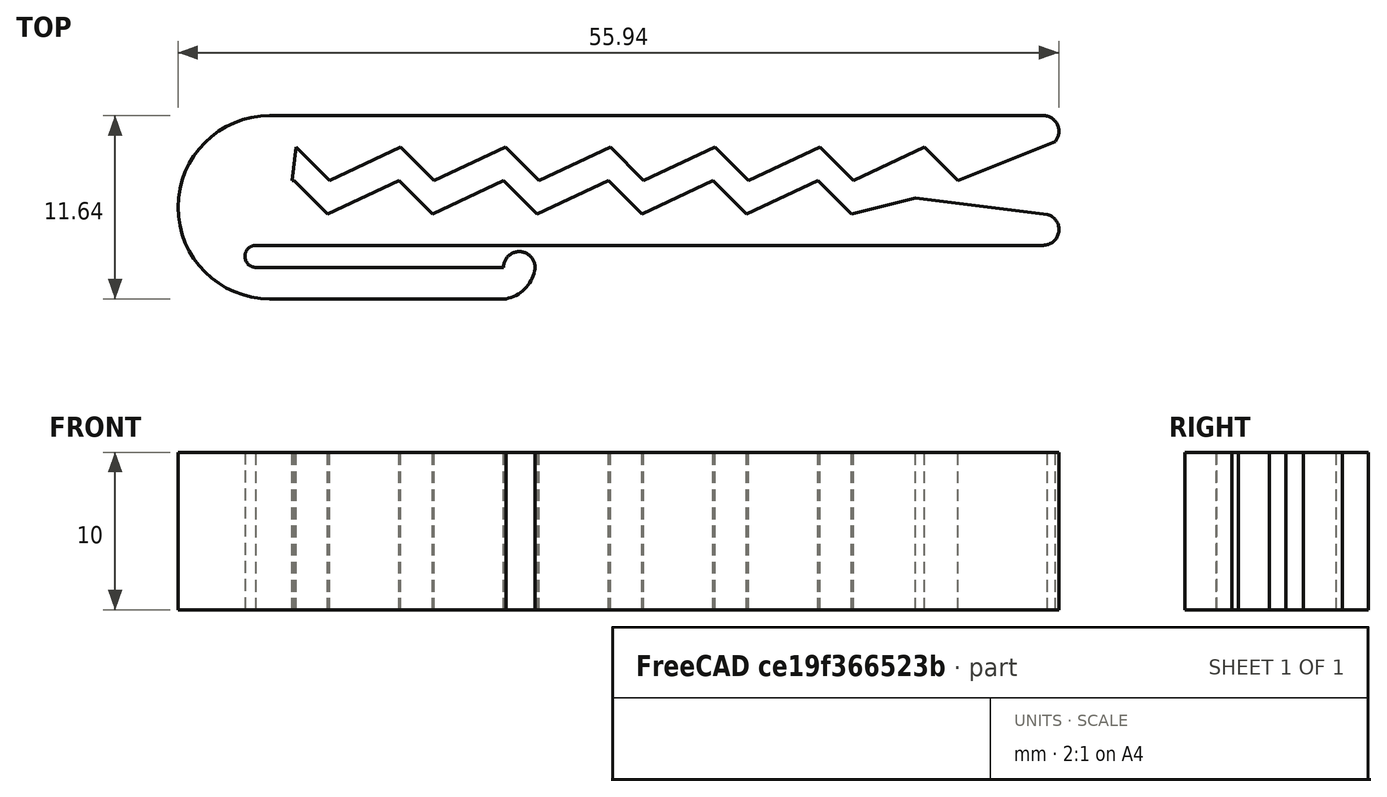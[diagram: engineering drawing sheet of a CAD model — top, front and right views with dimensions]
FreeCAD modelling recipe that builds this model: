
FCSTD DOCUMENT  (FreeCAD 0.20R29603 (Git))
Label: stipaljka_v2
License: All rights reserved
LicenseURL: http://en.wikipedia.org/wiki/All_rights_reserved
objects: Sketcher::SketchObject×1, PartDesign::Pad×1, PartDesign::Body×1
note: 4 computed .brp shape members not serialized (recipe doc carries the construction recipe); baked Part::Feature solids carry a one-line shape summary decoded from their .brp

FEATURE [Sketcher::SketchObject] Sketch
  FullyConstrained = false
  MapMode = 5
  Support = -> [XY_Plane]
  sketch-geometry (42):
    g0: LineSegment StartX=50.9512 StartY=35.3209 StartZ=0 EndX=100.075 EndY=35.3209 EndZ=0
    g1: ArcOfCircle CenterX=100.075 CenterY=34.3209 CenterZ=0 NormalX=0 NormalY=0 NormalZ=1 AngleXU=0 Radius=1 StartAngle=5.57883 EndAngle=7.85398
    g2: LineSegment StartX=94.6631 StartY=31.2022 StartZ=0 EndX=92.5392 EndY=33.3209 EndZ=0
    g3: LineSegment StartX=92.5392 StartY=33.3209 StartZ=0 EndX=88.0102 EndY=31.2022 EndZ=0
    g4: LineSegment StartX=88.0102 StartY=31.2022 StartZ=0 EndX=85.8863 EndY=33.3209 EndZ=0
    g5: LineSegment StartX=85.8863 StartY=33.3209 StartZ=0 EndX=81.3574 EndY=31.2022 EndZ=0
    g6: LineSegment StartX=81.3574 StartY=31.2022 StartZ=0 EndX=79.2334 EndY=33.3209 EndZ=0
    g7: LineSegment StartX=79.2334 StartY=33.3209 StartZ=0 EndX=74.7045 EndY=31.2022 EndZ=0
    g8: LineSegment StartX=74.7045 StartY=31.2022 StartZ=0 EndX=72.5806 EndY=33.3209 EndZ=0
    g9: LineSegment StartX=72.5806 StartY=33.3209 StartZ=0 EndX=68.0516 EndY=31.2022 EndZ=0
    g10: LineSegment StartX=68.0516 StartY=31.2022 StartZ=0 EndX=65.9277 EndY=33.3209 EndZ=0
    g11: LineSegment StartX=65.9277 StartY=33.3209 StartZ=0 EndX=61.3988 EndY=31.2022 EndZ=0
    g12: LineSegment StartX=61.3988 StartY=31.2022 StartZ=0 EndX=59.2748 EndY=33.3209 EndZ=0
    g13: LineSegment StartX=59.2748 StartY=33.3209 StartZ=0 EndX=54.7459 EndY=31.2022 EndZ=0
    g14: LineSegment StartX=54.7459 StartY=31.2022 StartZ=0 EndX=52.622 EndY=33.3209 EndZ=0
    g15: LineSegment StartX=48.5831 StartY=31.2022 StartZ=0 EndX=95.0691 EndY=31.2022 EndZ=0
    g16: LineSegment StartX=51.8061 StartY=29.0835 StartZ=0 EndX=101.005 EndY=29.0835 EndZ=0
    g17: LineSegment StartX=52.502 StartY=31.2022 StartZ=0 EndX=54.6259 EndY=29.0835 EndZ=0
    g18: LineSegment StartX=54.6259 StartY=29.0835 StartZ=0 EndX=59.1548 EndY=31.2022 EndZ=0
    g19: LineSegment StartX=59.1548 StartY=31.2022 StartZ=0 EndX=61.2788 EndY=29.0835 EndZ=0
    g20: LineSegment StartX=61.2788 StartY=29.0835 StartZ=0 EndX=65.8077 EndY=31.2022 EndZ=0
    g21: LineSegment StartX=65.8077 StartY=31.2022 StartZ=0 EndX=67.9316 EndY=29.0835 EndZ=0
    g22: LineSegment StartX=67.9316 StartY=29.0835 StartZ=0 EndX=72.4606 EndY=31.2022 EndZ=0
    g23: LineSegment StartX=72.4606 StartY=31.2022 StartZ=0 EndX=74.5845 EndY=29.0835 EndZ=0
    g24: LineSegment StartX=74.5845 StartY=29.0835 StartZ=0 EndX=79.1134 EndY=31.2022 EndZ=0
    g25: LineSegment StartX=79.1134 StartY=31.2022 StartZ=0 EndX=81.2374 EndY=29.0835 EndZ=0
    g26: LineSegment StartX=81.2374 StartY=29.0835 StartZ=0 EndX=85.7663 EndY=31.2022 EndZ=0
    g27: LineSegment StartX=85.7663 StartY=31.2022 StartZ=0 EndX=87.8902 EndY=29.0835 EndZ=0
    g28: LineSegment StartX=87.8902 StartY=29.0835 StartZ=0 EndX=91.9468 EndY=30.0995 EndZ=0
    g29: LineSegment StartX=52.622 StartY=33.3209 StartZ=0 EndX=52.3603 EndY=31.2022 EndZ=0
    g30: LineSegment StartX=52.502 StartY=31.2022 StartZ=0 EndX=52.3603 EndY=31.2022 EndZ=0
    g31: ArcOfCircle CenterX=100.075 CenterY=28.0835 CenterZ=0 NormalX=0 NormalY=0 NormalZ=1 AngleXU=0 Radius=1 StartAngle=4.71239 EndAngle=7.57436
    g32: LineSegment StartX=100.075 StartY=27.0835 StartZ=0 EndX=67.7065 EndY=27.0835 EndZ=0
    g33: LineSegment StartX=94.6631 StartY=31.2022 StartZ=0 EndX=100.837 EndY=33.6734 EndZ=0
    g34: LineSegment StartX=91.9468 StartY=30.0995 StartZ=0 EndX=100.351 EndY=29.0447 EndZ=0
    g35: LineSegment StartX=67.7065 StartY=27.0835 StartZ=0 EndX=50.0749 EndY=27.0835 EndZ=0
    g36: ArcOfCircle CenterX=50.0749 CenterY=26.3835 CenterZ=0 NormalX=0 NormalY=0 NormalZ=1 AngleXU=0 Radius=0.7 StartAngle=1.5708 EndAngle=4.73823
    g37: LineSegment StartX=50.093 StartY=25.6838 StartZ=0 EndX=65.8029 EndY=25.6838 EndZ=0
    g38: ArcOfCircle CenterX=66.8029 CenterY=25.6838 CenterZ=0 NormalX=0 NormalY=0 NormalZ=1 AngleXU=0 Radius=1 StartAngle=6.07315 EndAngle=9.42478
    g39: ArcOfCircle CenterX=65.5163 CenterY=25.958 CenterZ=0 NormalX=0 NormalY=0 NormalZ=1 AngleXU=0 Radius=2.31547 StartAngle=4.90132 EndAngle=6.07315
    g40: LineSegment StartX=65.9512 StartY=23.6838 StartZ=0 EndX=50.9512 EndY=23.6838 EndZ=0
    g41: ArcOfCircle CenterX=50.9512 CenterY=29.5023 CenterZ=0 NormalX=0 NormalY=0 NormalZ=1 AngleXU=0 Radius=5.81858 StartAngle=1.5708 EndAngle=4.71239
  constraints (114):
    c: Horizontal(g0)
    c: Diameter(g1) = 2
    c: Tangent(g1,g0) = 1.5708
    c: Coincident(g2,g3)
    c: Coincident(g3,g4)
    c: Coincident(g4,g5)
    c: Coincident(g5,g6)
    c: Coincident(g6,g7)
    c: Coincident(g7,g8)
    c: Coincident(g8,g9)
    c: Coincident(g9,g10)
    c: Coincident(g10,g11)
    c: Coincident(g11,g12)
    c: Coincident(g12,g13)
    c: Coincident(g13,g14)
    c: Equal(g13,g11)
    c: Equal(g11,g9)
    c: Equal(g9,g7)
    c: Equal(g7,g5)
    c: Equal(g5,g3)
    c: Parallel(g13,g11)
    c: Parallel(g11,g9)
    c: Parallel(g9,g7)
    c: Parallel(g7,g5)
    c: Parallel(g5,g3)
    c: Distance(g3) = 5
    c: Equal(g2,g4)
    c: Equal(g4,g6)
    c: Equal(g6,g8)
    c: Equal(g8,g10)
    c: Equal(g10,g12)
    c: Equal(g12,g14)
    c: Parallel(g14,g12)
    c: Parallel(g12,g10)
    c: Parallel(g10,g8)
    c: Parallel(g8,g6)
    c: Parallel(g6,g4)
    c: Parallel(g4,g2)
    c: PointOnObject(g2,g15)
    c: PointOnObject(g3,g15)
    c: Angle(g3,g2) = 1.91986
    c: Distance(g4) = 3
    c: DistanceY(g2,g0) = 2
    c: Horizontal(g16)
    c: PointOnObject(g17,g16)
    c: Coincident(g17,g18)
    c: Coincident(g18,g19)
    c: PointOnObject(g19,g16)
    c: Coincident(g19,g20)
    c: Coincident(g20,g21)
    c: PointOnObject(g21,g16)
    c: Coincident(g21,g22)
    c: Coincident(g22,g23)
    c: PointOnObject(g23,g16)
    c: Coincident(g23,g24)
    c: Coincident(g24,g25)
    c: PointOnObject(g25,g16)
    c: Coincident(g25,g26)
    c: Coincident(g26,g27)
    c: PointOnObject(g27,g16)
    c: Coincident(g27,g28)
    c: Equal(g18,g20)
    c: Equal(g20,g22)
    c: Equal(g22,g24)
    c: Equal(g24,g26)
    c: Parallel(g26,g24)
    c: Parallel(g24,g22)
    c: Parallel(g22,g20)
    c: Parallel(g20,g18)
    c: Equal(g17,g19)
    c: Equal(g19,g21)
    c: Equal(g21,g23)
    c: Equal(g23,g25)
    c: Equal(g25,g27)
    c: Parallel(g17,g19)
    c: Angle(g22,g23) = 1.91986
    c: Distance(g18) = 5
    c: Distance(g21) = 3
    c: Coincident(g29,g14)
    c: PointOnObject(g29,g15)
    c: Coincident(g30,g17)
    c: Coincident(g30,g29)
    c: Equal(g31,g1)
    c: Tangent(g31,g32) = 1.5708
    c: DistanceY(g26,g3) = 0
    c: Horizontal(g15)
    c: Horizontal(g32)
    c: Coincident(g33,g2)
    c: Coincident(g33,g1)
    c: Coincident(g34,g28)
    c: Coincident(g34,g31)
    c: DistanceY(g31,g27) = 2
    c: DistanceX(g31,g1) = 0
    c: DistanceX(g17,g13) = 0.12
    c: Angle(g28,g27) = 2.11202
    c: Distance(g34) = 8.47
    c: Distance(g33) = 6.65
    c: Coincident(g32,g35)
    c: Horizontal(g35)
    c: Tangent(g35,g36) = -1.5708
    c: Coincident(g36,g37)
    c: Horizontal(g37)
    c: Perpendicular(g37,g38) = 4.71239
    c: Tangent(g38,g39) = -1.5708
    c: Coincident(g39,g40)
    c: Horizontal(g40)
    c: Tangent(g40,g41) = 1.5708
    c: Coincident(g41,g0)
    c: Diameter(g36) = 1.4
    c: Diameter(g38) = 2
    c: DistanceX(g35,g31) = 50
    c: DistanceX(g40,g40) = 15
    c: DistanceY(g39,g37) = 2
    c: DistanceX(g0,g41) = 0
FEATURE [PartDesign::Pad] Pad
  Direction = (0,0,1)
  Length = 10
  Length2 = 10
  Profile = -> Sketch
  ReferenceAxis = -> Sketch [N_Axis]
  Type = 0
FEATURE [PartDesign::Body] Body
  Group = -> [Sketch,Pad]
  Origin = -> Origin
  Tip = -> Pad
